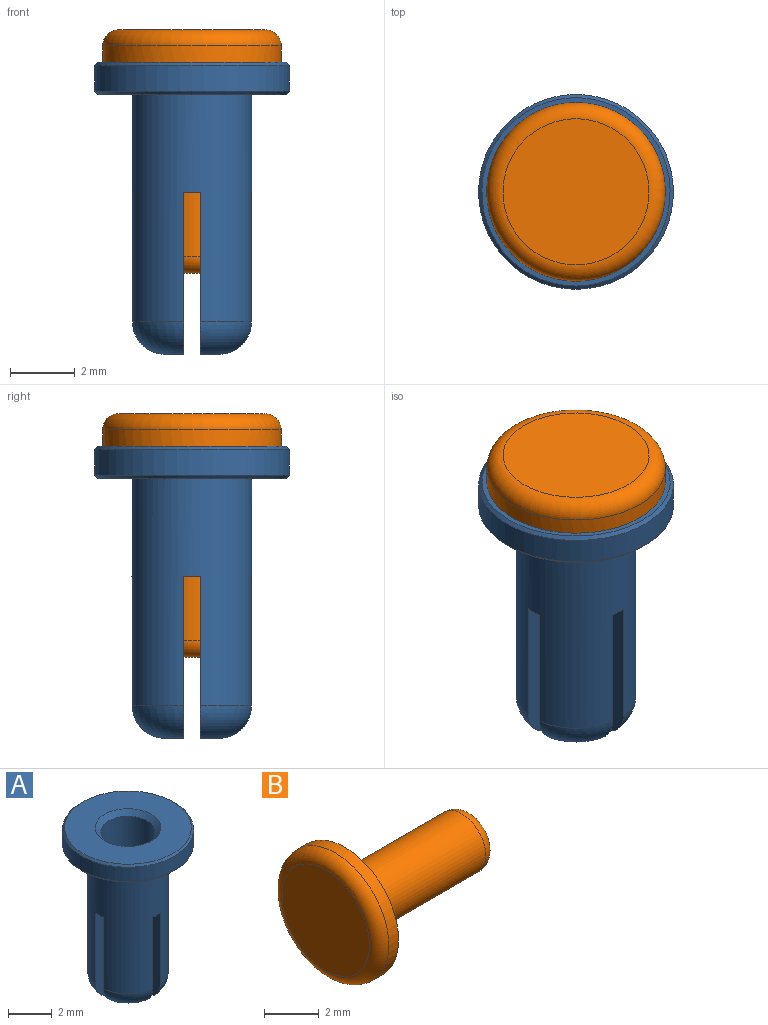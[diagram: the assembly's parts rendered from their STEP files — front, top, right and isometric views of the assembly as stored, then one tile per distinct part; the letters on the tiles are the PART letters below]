
ASSEMBLY  parts=2 mates=1
PART A: 32 faces, bbox 6.3x6.3x9.3 mm
  f0: cone r=1.25mm half-angle=45deg, axis (0,0,1), area 3.1mm2, adj f4,f27
  f1: cone r=2.9mm half-angle=45deg, axis (0,0,-1), area 2.6mm2, adj f3,f27
  f2: cone r=3mm half-angle=45deg, axis (0,0,1), area 2.6mm2, adj f3,f26
  f3: cylinder r=3mm len=6mm, axis (0,0,-1), area 15.1mm2, adj f1,f2
  f4: cylinder r=1.25mm len=4.75mm, axis (0,0,1), area 35.3mm2, adj f0,f9,f10,f11,f13,f14,f15,f16
  f5: cylinder r=1.85mm len=7mm, axis (0,0,-1), area 73.3mm2, adj f14,f15,f16,f17,f18,f19,f20,f21
  f6: plane 0.56x0.56mm, normal (0,0,-1), area 0.2mm2, adj f18,f19,f29
  f7: plane 0.56x0.56mm, normal (0,0,-1), area 0.2mm2, adj f20,f21,f28
  f8: plane 0.56x0.56mm, normal (0,0,-1), area 0.2mm2, adj f22,f23,f31
  f9: cone r=0.35mm half-angle=30deg, axis (0,0,1), area 1mm2, adj f4,f18,f19
  f10: cone r=0.35mm half-angle=30deg, axis (0,0,1), area 1mm2, adj f4,f20,f21
  f11: cone r=0.35mm half-angle=30deg, axis (0,0,1), area 1mm2, adj f4,f22,f23
  f12: plane 0.56x0.56mm, normal (0,0,-1), area 0.2mm2, adj f24,f25,f30
  f13: cone r=0.35mm half-angle=30deg, axis (0,0,1), area 1mm2, adj f4,f24,f25
  f14: plane 0.63x0.5mm, normal (0,0,-1), area 0.3mm2, adj f4,f5,f23,f24
  f15: plane 0.63x0.5mm, normal (0,0,-1), area 0.3mm2, adj f4,f5,f18,f25
  f16: plane 0.63x0.5mm, normal (0,0,-1), area 0.3mm2, adj f4,f5,f19,f20
  f17: plane 0.63x0.5mm, normal (0,0,-1), area 0.3mm2, adj f4,f5,f21,f22
  f18: plane 5.29x1.88mm, normal (1,0,0), area 5.9mm2, adj f4,f5,f6,f9,f15,f19,f29
  f19: plane 5.29x1.88mm, normal (0,-1,0), area 5.9mm2, adj f4,f5,f6,f9,f16,f18,f29
  f20: plane 5.29x1.88mm, normal (0,1,0), area 5.9mm2, adj f4,f5,f7,f10,f16,f21,f28
  f21: plane 5.29x1.88mm, normal (1,0,0), area 5.9mm2, adj f4,f5,f7,f10,f17,f20,f28
  f22: plane 5.29x1.88mm, normal (-1,0,0), area 5.9mm2, adj f4,f5,f8,f11,f17,f23,f31
  f23: plane 5.29x1.88mm, normal (0,1,0), area 5.9mm2, adj f4,f5,f8,f11,f14,f22,f31
  f24: plane 5.29x1.88mm, normal (0,-1,0), area 5.9mm2, adj f4,f5,f12,f13,f14,f25,f30
  f25: plane 5.29x1.88mm, normal (-1,0,0), area 5.9mm2, adj f4,f5,f12,f13,f15,f24,f30
  f26: plane 5.8x5.8mm, normal (0,0,-1), area 15.7mm2, adj f2,f5
  f27: plane 5.8x5.8mm, normal (0,0,1), area 19.4mm2, adj f0,f1
  f28: torus R=0.85mm, axis (0,0,1), area 2.7mm2, adj f5,f7,f20,f21
  f29: torus R=0.85mm, axis (0,0,1), area 2.7mm2, adj f5,f6,f18,f19
  f30: torus R=0.85mm, axis (0,0,1), area 2.7mm2, adj f5,f12,f24,f25
  f31: torus R=0.85mm, axis (0,0,1), area 2.7mm2, adj f5,f8,f22,f23
PART B: 7 faces, bbox 7.5x6x6 mm
  f0: torus R=2.25mm, axis (1,0,0), area 12.7mm2, adj f2,f6
  f1: torus R=0.75mm, axis (-1,0,0), area 5.3mm2, adj f3,f4
  f2: cylinder r=2.75mm len=5.5mm, axis (-1,0,0), area 8.6mm2, adj f0,f5
  f3: cylinder r=1.25mm len=6mm, axis (-1,0,0), area 47.1mm2, adj f1,f5
  f4: plane 1.5x1.5mm, normal (1,0,0), area 1.8mm2, adj f1
  f5: plane 5.5x5.5mm, normal (1,0,0), area 18.8mm2, adj f2,f3
  f6: plane 4.5x4.5mm, normal (-1,0,0), area 15.9mm2, adj f0
PLACE A t=(0,0,4)mm
PLACE B rot(axis=(0.71,0,-0.71),180deg) t=(0,-1.25,2.5)mm
MATE fastened B.f0 <-> A.f0  axis (0,0,-1) through (0,0,9)mm
